# Revit family: QF_Woodson_Module Square Cold Food Display_W.CFSQ23_W.CFSQ24
name_source: partatom
category: Specialty Equipment
revit_build: Autodesk Revit MEP 2014 (Build: 20140709_2115(x64)
units: mm (PartAtom-declared; Revit-internal decimal feet)

## types (2) — shared parameters
Assembly Code = E1090300
Body = QF_Stainless-Polished
Cooling Box Height = 411.2 mm  [stored 1.34908 ft]
Depth = 605 mm  [stored 1.98491 ft]
Description = Square Profile Cold Food Display
Drain Connector = 20 mm  [stored 0.0656168 ft]
FL Amps = 10 A
Glass = QF_Glass_Transparent
Handle = QF_Plastic-Black-Coarse
Height = 1142.9 mm  [stored 3.74967 ft]
Manufacturer = Woodson
Type Comments = The ever popular square profile design provides optimal product display and suits modern styling, while LED lighting ensure smaximum product display at all times.
URL = http://www.stoddart.com.au
Volts = 240 V
Watts = 2400 W

## per-type parameters (varying)
| type | Box Height | Number Of Modules | Weight | Width |
| W.CFSQ23 | 180.8 mm | 2 | 190.00 kg | 1166 mm |
| W.CFSQ24 | 220.8 mm | 3 | 230.00 kg | 1500 mm  [stored 4.92126 ft] |

note: column(s) folded — value = type name in every type: Model

note: [stored X ft] marks values corroborated as IEEE doubles in the binary element streams (Revit-internal decimal feet)

## geometry (parser evidence)
native form markers: Sweep x1
no freeform markers — native parametric forms only
